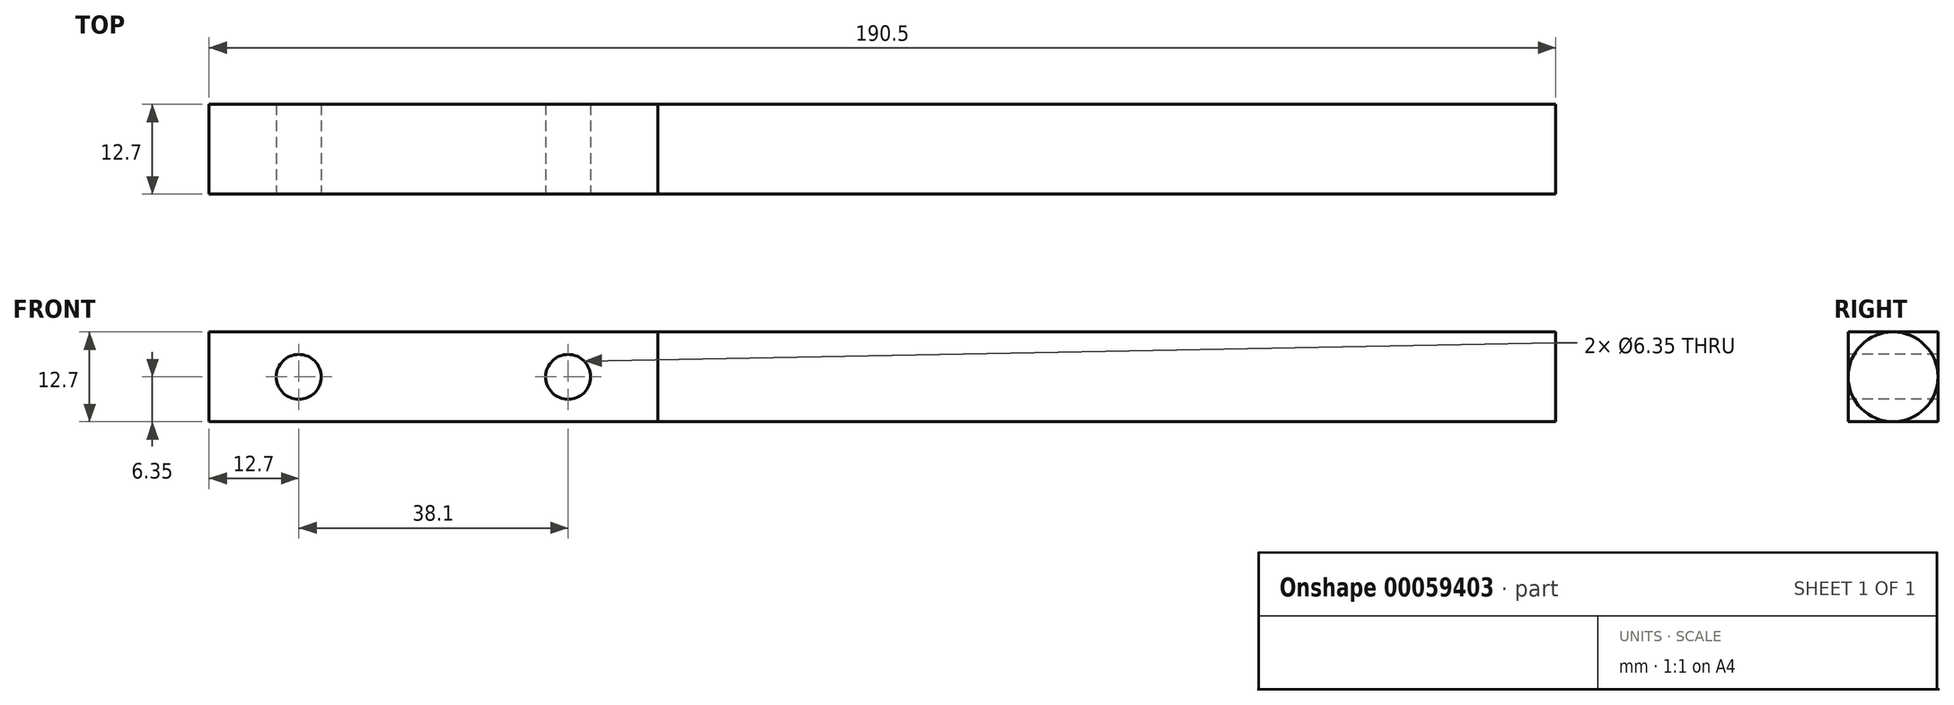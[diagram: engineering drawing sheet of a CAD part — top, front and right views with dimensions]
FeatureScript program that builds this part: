
annotation { "Feature Type Name" : "Feature", "Feature Type Description" : "" }
export const myFeature = defineFeature(function(context is Context, id is Id, definition is map)
    precondition{}
    {
        {
            var Q0;
            Q0=qCreatedBy(makeId("Right.planeOp"),FACE);
            var sketch = newSketch(context, id + "F0", { "sketchPlane" : qUnion([Q0])});
            skCircle(sketch, "E0", {"center": v(0, 0) * mm, "radius": 6.35 * mm});
            skSolve(sketch);
        }
        {
            var Q0;
            Q0 = qSketchRegion(id + "F0", true);
            extrude(context, id + "F1", {"entities" : qUnion([Q0]), "depth" : 127 * mm});
        }
        {
            var Q0;
            Q0=qCreatedBy(makeId("Right.planeOp"),FACE);
            var sketch = newSketch(context, id + "F2", { "sketchPlane" : qUnion([Q0])});
            skLineSegment(sketch, "E1.bottom", {"start": v(6.35, -6.35) * mm, "end": v(-6.35, -6.35) * mm});
            skLineSegment(sketch, "E1.top", {"start": v(6.35, 6.35) * mm, "end": v(-6.35, 6.35) * mm});
            skLineSegment(sketch, "E1.left", {"start": v(6.35, -6.35) * mm, "end": v(6.35, 6.35) * mm});
            skLineSegment(sketch, "E1.right", {"start": v(-6.35, -6.35) * mm, "end": v(-6.35, 6.35) * mm});
            skSolve(sketch);
        }
        {
            var Q0;
            Q0 = qSketchRegion(id + "F2", true);
            extrude(context, id + "F3", {"entities" : qUnion([Q0]), "operationType" : NewBodyOperationType.ADD, "oppositeDirection" : true, "depth" : 63.5 * mm});
        }
        {
            var Q0;
            Q0=makeQuery(id+"F3.opExtrude","SWEPT_FACE",FACE,{"disambiguationData":[OSD([sQuery(id+"F2.wireOp",EDGE,"E1.right")])]});
            var sketch = newSketch(context, id + "F4", { "sketchPlane" : qUnion([Q0])});
            skCircle(sketch, "E2", {"center": v(-50.8, 0) * mm, "radius": 3.18 * mm});
            skCircle(sketch, "E3", {"center": v(-12.7, 0) * mm, "radius": 3.18 * mm});
            skSolve(sketch);
        }
        {
            var Q0;
            Q0 = qSketchRegion(id + "F4", true);
            extrude(context, id + "F5", {"entities" : qUnion([Q0]), "operationType" : NewBodyOperationType.REMOVE, "endBound" : BoundingType.THROUGH_ALL, "oppositeDirection" : true, "depth" : 25.4 * mm});
        }
    });
